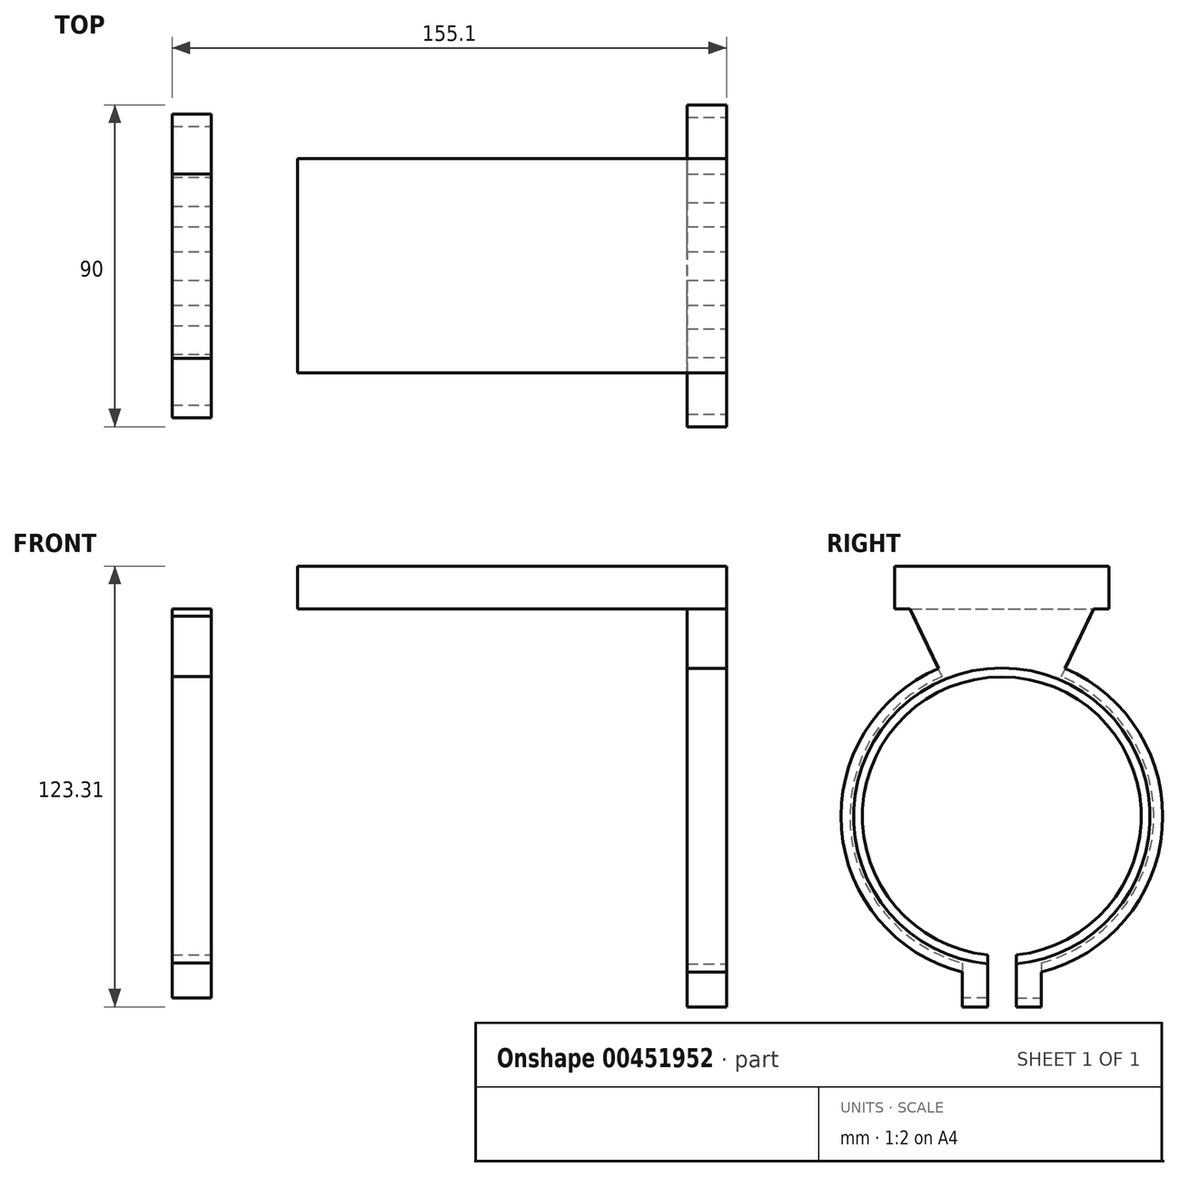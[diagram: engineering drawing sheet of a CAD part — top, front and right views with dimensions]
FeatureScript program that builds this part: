
annotation { "Feature Type Name" : "Feature", "Feature Type Description" : "" }
export const myFeature = defineFeature(function(context is Context, id is Id, definition is map)
    precondition{}
    {
        {
            var Q0;
            Q0=qCreatedBy(makeId("Top.planeOp"),FACE);
            var sketch = newSketch(context, id + "F0", { "sketchPlane" : qUnion([Q0])});
            skCircle(sketch, "E0", {"center": v(-45, 17.5) * mm, "radius": 3.25 * mm});
            skCircle(sketch, "E1", {"center": v(45, 17.5) * mm, "radius": 3.25 * mm});
            skCircle(sketch, "E2", {"center": v(45, -17.5) * mm, "radius": 3.25 * mm});
            skCircle(sketch, "E3", {"center": v(-45, -17.5) * mm, "radius": 3.25 * mm});
            skSolve(sketch);
        }
        {
            var Q0;
            Q0=sQuery(id+"F0.wireOp",EDGE,"E0");
            var Q1;
            Q1=sQuery(id+"F0.wireOp",EDGE,"E1");
            var Q2;
            Q2=sQuery(id+"F0.wireOp",EDGE,"E2");
            var Q3;
            Q3=sQuery(id+"F0.wireOp",EDGE,"E3");
            extrude(context, id + "F1", {"bodyType" : ToolBodyType.SURFACE, "surfaceEntities" : qUnion([Q0, Q1, Q2, Q3]), "depth" : 12 * mm});
        }
        {
            var Q0;
            Q0=qCreatedBy(makeId("Top.planeOp"),FACE);
            var sketch = newSketch(context, id + "F2", { "sketchPlane" : qUnion([Q0])});
            skLineSegment(sketch, "E4.bottom", {"start": v(-67, -30) * mm, "end": v(53, -30) * mm});
            skLineSegment(sketch, "E4.top", {"start": v(-67, 30) * mm, "end": v(53, 30) * mm});
            skLineSegment(sketch, "E4.left", {"start": v(-67, -30) * mm, "end": v(-67, 30) * mm});
            skLineSegment(sketch, "E4.right", {"start": v(53, -30) * mm, "end": v(53, 30) * mm});
            skSolve(sketch);
        }
        {
            var Q0;
            Q0=makeQuery(id+"F2.imprint","IMPRINT",FACE,{"disambiguationData":[TD([[makeQuery(id+"F2.imprint","IMPRINT",EDGE,{"derivedFrom":sQuery(id+"F2.wireOp",EDGE,"E4.bottom")}),1.0]])]});
            extrude(context, id + "F3", {"entities" : qUnion([Q0]), "oppositeDirection" : true, "depth" : 12 * mm});
        }
        {
            var Q0;
            Q0=makeQuery(id+"F3.opExtrude","SWEPT_FACE",FACE,{"disambiguationData":[OSD([sQuery(id+"F2.wireOp",EDGE,"E4.right")])]});
            var sketch = newSketch(context, id + "F4", { "sketchPlane" : qUnion([Q0])});
            skArc(sketch, "E5", {"start": v(4, -111.3) * mm, "mid": v(0, -28.5) * mm, "end": v(-4, -111.3) * mm});
            skArc(sketch, "E6", {"start": v(4, -114.82) * mm, "mid": v(0, -25) * mm, "end": v(-4, -114.82) * mm});
            skLineSegment(sketch, "E7", {"start": v(17.67, -28.61) * mm, "end": v(25.76, -11.77) * mm});
            skLineSegment(sketch, "E8", {"start": v(25.76, -11.77) * mm, "end": v(0, -11.77) * mm});
            skLineSegment(sketch, "E9.MirrorCS", {"start": v(-25.76, -11.77) * mm, "end": v(0, -11.77) * mm});
            skLineSegment(sketch, "E10.MirrorCS", {"start": v(-17.67, -28.61) * mm, "end": v(-25.76, -11.77) * mm});
            skLineSegment(sketch, "E11", {"start": v(0, -73.77) * mm, "end": v(0, -139.64) * mm, "construction": true});
            skLineSegment(sketch, "E12.bottom", {"start": v(4, -111.3) * mm, "end": v(11, -111.3) * mm});
            skLineSegment(sketch, "E12.top", {"start": v(4, -123.3) * mm, "end": v(11, -123.3) * mm});
            skLineSegment(sketch, "E12.left", {"start": v(4, -111.3) * mm, "end": v(4, -123.3) * mm});
            skLineSegment(sketch, "E12.right", {"start": v(11, -111.3) * mm, "end": v(11, -123.3) * mm});
            skLineSegment(sketch, "E13.MirrorCS", {"start": v(-4, -123.3) * mm, "end": v(-11, -123.3) * mm});
            skLineSegment(sketch, "E14.MirrorCS", {"start": v(-4, -111.3) * mm, "end": v(-4, -123.3) * mm});
            skLineSegment(sketch, "E15.MirrorCS", {"start": v(-4, -111.3) * mm, "end": v(-11, -111.3) * mm});
            skLineSegment(sketch, "E16.MirrorCS", {"start": v(-11, -111.3) * mm, "end": v(-11, -123.3) * mm});
            skSolve(sketch);
        }
        {
            var Q0;
            {var subQ0=sQuery(id+"F4.wireOp",EDGE,"E7");Q0=makeQuery(id+"F4.imprint","IMPRINT",FACE,{"disambiguationData":[TD([[makeQuery(id+"F4.imprint","IMPRINT",EDGE,{"derivedFrom":subQ0}),1.0]])]});}
            var Q1;
            Q1=makeQuery(id+"F4.imprint","IMPRINT",FACE,{"disambiguationData":[TD([[makeQuery(id+"F4.imprint","IMPRINT",EDGE,{"derivedFrom":sQuery(id+"F4.wireOp",EDGE,"E5")}),-1.0]])]});
            var Q2;
            {var subQ5=sQuery(id+"F4.wireOp",EDGE,"E13.MirrorCS");Q2=makeQuery(id+"F4.imprint","IMPRINT",FACE,{"disambiguationData":[TD([[makeQuery(id+"F4.imprint","IMPRINT",EDGE,{"derivedFrom":subQ5}),-1.0]])]});}
            var Q3;
            {var subQ5=sQuery(id+"F4.wireOp",EDGE,"E12.top");Q3=makeQuery(id+"F4.imprint","IMPRINT",FACE,{"disambiguationData":[TD([[makeQuery(id+"F4.imprint","IMPRINT",EDGE,{"derivedFrom":subQ5}),1.0]])]});}
            var Q4;
            {var subQ5=sQuery(id+"F4.wireOp",EDGE,"E12.bottom");Q4=makeQuery(id+"F4.imprint","IMPRINT",FACE,{"disambiguationData":[TD([[makeQuery(id+"F4.imprint","IMPRINT",EDGE,{"derivedFrom":subQ5}),-1.0]])]});}
            var Q5;
            {var subQ5=sQuery(id+"F4.wireOp",EDGE,"E15.MirrorCS");Q5=makeQuery(id+"F4.imprint","IMPRINT",FACE,{"disambiguationData":[TD([[makeQuery(id+"F4.imprint","IMPRINT",EDGE,{"derivedFrom":subQ5}),1.0]])]});}
            var Q6;
            Q6 = qSketchRegion(id + "F6", true);
            extrude(context, id + "F5", {"entities" : qUnion([Q0, Q1, Q2, Q3, Q4, Q5, Q6]), "operationType" : NewBodyOperationType.ADD, "oppositeDirection" : true, "depth" : 11 * mm});
        }
        {
            var Q0;
            Q0=makeQuery(id+"F3.opExtrude","SWEPT_FACE",FACE,{"disambiguationData":[OSD([sQuery(id+"F2.wireOp",EDGE,"E4.left")])]});
            var sketch = newSketch(context, id + "F6", { "sketchPlane" : qUnion([Q0])});
            skArc(sketch, "E17", {"start": v(4, -108.8) * mm, "mid": v(0, -31) * mm, "end": v(-4, -108.8) * mm});
            skArc(sketch, "E18", {"start": v(4, -112.31) * mm, "mid": v(0, -27.5) * mm, "end": v(-4, -112.31) * mm});
            skLineSegment(sketch, "E19", {"start": v(16.69, -30.91) * mm, "end": v(24.78, -14.07) * mm});
            skLineSegment(sketch, "E20.bottom", {"start": v(4, -108.8) * mm, "end": v(11, -108.8) * mm});
            skLineSegment(sketch, "E20.top", {"start": v(4, -120.8) * mm, "end": v(11, -120.8) * mm});
            skLineSegment(sketch, "E20.left", {"start": v(4, -108.8) * mm, "end": v(4, -120.8) * mm});
            skLineSegment(sketch, "E20.right", {"start": v(11, -108.8) * mm, "end": v(11, -120.8) * mm});
            skLineSegment(sketch, "E21.MirrorCS", {"start": v(-4, -108.8) * mm, "end": v(-4, -120.8) * mm});
            skLineSegment(sketch, "E22.MirrorCS", {"start": v(-4, -108.8) * mm, "end": v(-11, -108.8) * mm});
            skLineSegment(sketch, "E23.MirrorCS", {"start": v(-16.69, -30.91) * mm, "end": v(-24.78, -14.07) * mm});
            skPoint(sketch, "E24.orphan", {"position": v(-0.98, -12.14) * mm});
            skPoint(sketch, "E25.end.orphan", {"position": v(0.98, -12.14) * mm});
            skPoint(sketch, "E26.MirrorCS.start.orphan", {"position": v(-24.78, -12.14) * mm});
            skLineSegment(sketch, "E27", {"start": v(24.78, -14.07) * mm, "end": v(25.83, -12) * mm});
            skLineSegment(sketch, "E28", {"start": v(-24.78, -14.07) * mm, "end": v(-25.74, -12) * mm});
            skPoint(sketch, "E29.end.orphan", {"position": v(0, -12.14) * mm});
            skLineSegment(sketch, "E30", {"start": v(-25.74, -12) * mm, "end": v(25.83, -12) * mm});
            skLineSegment(sketch, "E31", {"start": v(-4, -114.8) * mm, "end": v(4, -114.8) * mm, "construction": true});
            skLineSegment(sketch, "E32", {"start": v(4, -114.8) * mm, "end": v(0, -114.8) * mm, "construction": true});
            skLineSegment(sketch, "E33", {"start": v(0, -114.8) * mm, "end": v(0, -99.8) * mm, "construction": true});
            skLineSegment(sketch, "E34.trimOffspring", {"start": v(-11, -111.05) * mm, "end": v(-11, -118.86) * mm});
            skLineSegment(sketch, "E35.MirrorCS", {"start": v(-11, -108.8) * mm, "end": v(-11, -120.8) * mm});
            skLineSegment(sketch, "E36.MirrorCS", {"start": v(-4, -120.8) * mm, "end": v(-11, -120.8) * mm});
            skSolve(sketch);
        }
        {
            var Q0;
            Q0=makeQuery(id+"F6.imprint","IMPRINT",FACE,{"disambiguationData":[TD([[makeQuery(id+"F6.imprint","IMPRINT",EDGE,{"derivedFrom":sQuery(id+"F6.wireOp",EDGE,"E17")}),-1.0]])]});
            var Q1;
            {var subQ5=sQuery(id+"F6.wireOp",EDGE,"E22.MirrorCS");Q1=makeQuery(id+"F6.imprint","IMPRINT",FACE,{"disambiguationData":[TD([[makeQuery(id+"F6.imprint","IMPRINT",EDGE,{"derivedFrom":subQ5}),1.0]])]});}
            var Q2;
            {var subQ5=sQuery(id+"F6.wireOp",EDGE,"E36.MirrorCS");Q2=makeQuery(id+"F6.imprint","IMPRINT",FACE,{"disambiguationData":[TD([[makeQuery(id+"F6.imprint","IMPRINT",EDGE,{"derivedFrom":subQ5}),-1.0]])]});}
            var Q3;
            {var subQ5=sQuery(id+"F6.wireOp",EDGE,"E20.bottom");Q3=makeQuery(id+"F6.imprint","IMPRINT",FACE,{"disambiguationData":[TD([[makeQuery(id+"F6.imprint","IMPRINT",EDGE,{"derivedFrom":subQ5}),-1.0]])]});}
            var Q4;
            {var subQ5=sQuery(id+"F6.wireOp",EDGE,"E20.top");Q4=makeQuery(id+"F6.imprint","IMPRINT",FACE,{"disambiguationData":[TD([[makeQuery(id+"F6.imprint","IMPRINT",EDGE,{"derivedFrom":subQ5}),1.0]])]});}
            var Q5;
            {var subQ0=sQuery(id+"F6.wireOp",EDGE,"E19");Q5=makeQuery(id+"F6.imprint","IMPRINT",FACE,{"disambiguationData":[TD([[makeQuery(id+"F6.imprint","IMPRINT",EDGE,{"derivedFrom":subQ0}),1.0]])]});}
            extrude(context, id + "F7", {"entities" : qUnion([Q0, Q1, Q2, Q3, Q4, Q5]), "endBound" : BoundingType.SYMMETRIC, "depth" : 11 * mm});
        }
        {
            var Q0;
            Q0=makeQuery(id+"F7.opExtrude","SWEPT_BODY",BODY,{"disambiguationData":[OSD([sQuery(id+"F6.wireOp",EDGE,"E17"),sQuery(id+"F6.wireOp",EDGE,"E18"),sQuery(id+"F6.wireOp",EDGE,"E19"),sQuery(id+"F6.wireOp",EDGE,"E20.top"),sQuery(id+"F6.wireOp",EDGE,"E20.left"),sQuery(id+"F6.wireOp",EDGE,"E20.right"),sQuery(id+"F6.wireOp",EDGE,"E21.MirrorCS"),sQuery(id+"F6.wireOp",EDGE,"E23.MirrorCS"),sQuery(id+"F6.wireOp",EDGE,"E27"),sQuery(id+"F6.wireOp",EDGE,"E28"),sQuery(id+"F6.wireOp",EDGE,"E30"),sQuery(id+"F6.wireOp",EDGE,"E35.MirrorCS"),sQuery(id+"F6.wireOp",EDGE,"E36.MirrorCS")])]});
            transform(context, id + "F8", {"entities" : qUnion([Q0]), "transformType" : TransformType.TRANSLATION_3D, "dx" : -29.6 * mm, "dy" : 0 * mm, "dz" : 0 * mm, "makeCopy" : false});
        }
    });
